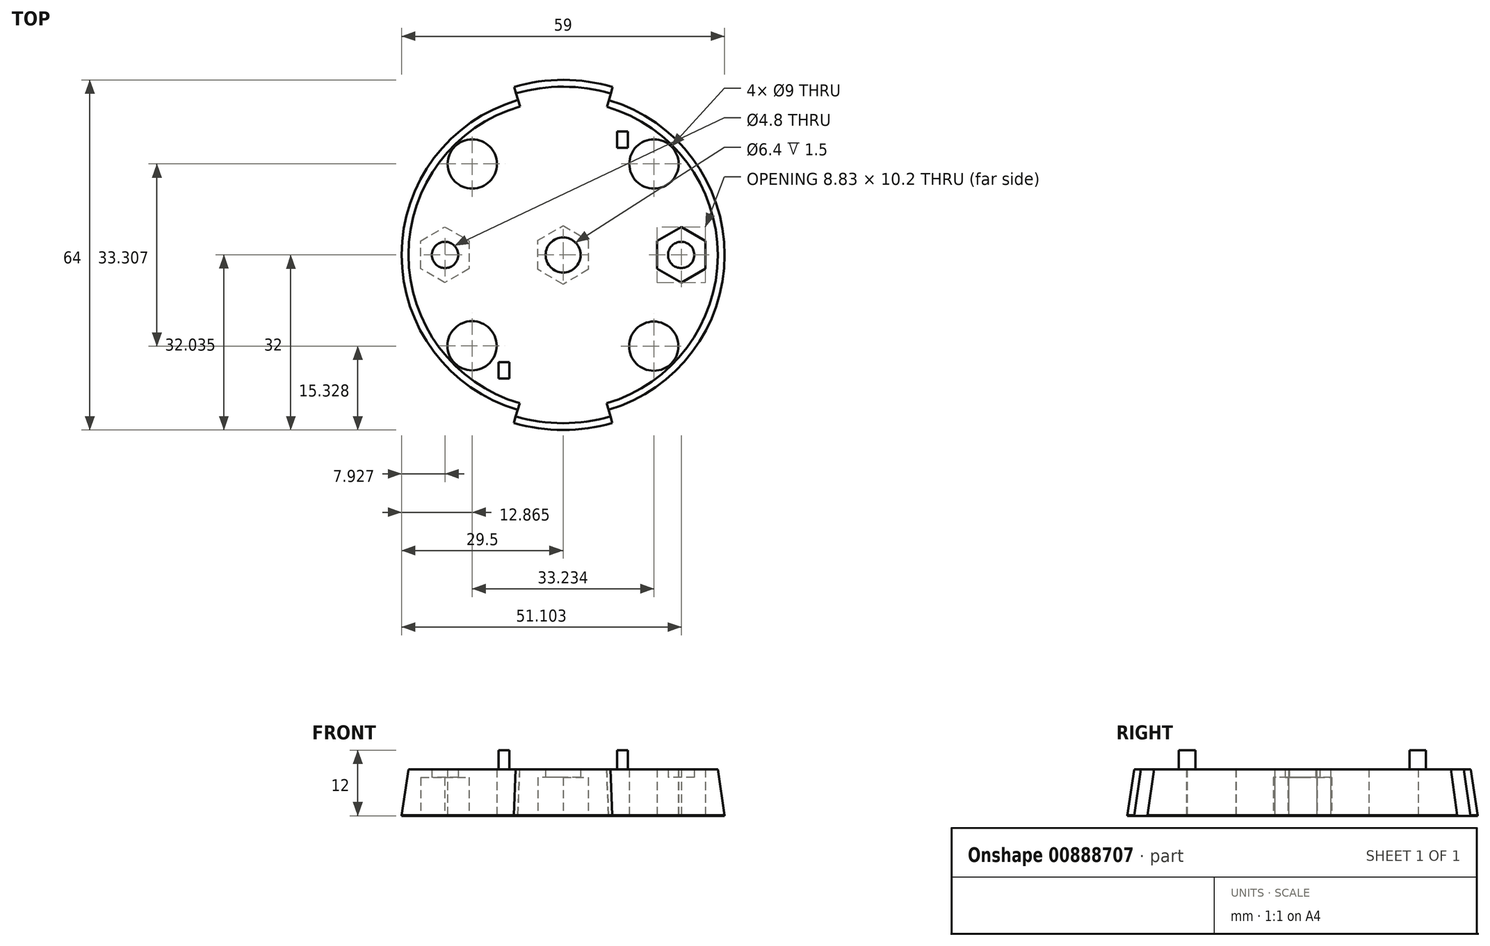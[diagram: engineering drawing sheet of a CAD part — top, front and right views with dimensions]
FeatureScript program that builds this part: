
annotation { "Feature Type Name" : "Feature", "Feature Type Description" : "" }
export const myFeature = defineFeature(function(context is Context, id is Id, definition is map)
    precondition{}
    {
        {
            var Q0;
            Q0=qCreatedBy(makeId("Top.planeOp"),FACE);
            var sketch = newSketch(context, id + "F0", { "sketchPlane" : qUnion([Q0])});
            skCircle(sketch, "E0", {"center": v(0, 0) * mm, "radius": 32 * mm});
            skCircle(sketch, "E1.cCircle", {"center": v(0, 0) * mm, "radius": 4.62 * mm, "construction": true});
            skLineSegment(sketch, "E1.0", {"start": v(4.62, 2.67) * mm, "end": v(4.62, -2.67) * mm});
            skLineSegment(sketch, "E1.1", {"start": v(4.62, -2.67) * mm, "end": v(0, -5.34) * mm});
            skLineSegment(sketch, "E1.2", {"start": v(0, -5.34) * mm, "end": v(-4.63, -2.67) * mm});
            skLineSegment(sketch, "E1.3", {"start": v(-4.62, -2.67) * mm, "end": v(-4.62, 2.67) * mm});
            skLineSegment(sketch, "E1.4", {"start": v(-4.63, 2.67) * mm, "end": v(0, 5.34) * mm});
            skLineSegment(sketch, "E1.5", {"start": v(0, 5.34) * mm, "end": v(4.62, 2.67) * mm});
            skPoint(sketch, "E1.0.midPoint", {"position": v(4.62, 0) * mm});
            skCircle(sketch, "E2", {"center": v(0, 0) * mm, "radius": 3.2 * mm});
            skCircle(sketch, "E3", {"center": v(0, 0) * mm, "radius": 29.5 * mm});
            skCircle(sketch, "E4", {"center": v(-29.5, 0) * mm, "radius": 4.3 * mm, "construction": true});
            skLineSegment(sketch, "E5", {"start": v(0, 5.34) * mm, "end": v(0, -5.34) * mm, "construction": true});
            skLineSegment(sketch, "E6", {"start": v(0, 0) * mm, "end": v(-35.07, 35.15) * mm, "construction": true});
            skLineSegment(sketch, "E7", {"start": v(0, 0) * mm, "end": v(-62.76, 0.07) * mm, "construction": true});
            skLineSegment(sketch, "E8", {"start": v(0, -32) * mm, "end": v(0, -45.25) * mm, "construction": true});
            skLineSegment(sketch, "E9", {"start": v(0, -45.25) * mm, "end": v(-9, -45.25) * mm, "construction": true});
            skLineSegment(sketch, "E10", {"start": v(-9, -45.25) * mm, "end": v(-9, -28.1) * mm, "construction": true});
            skCircle(sketch, "E11", {"center": v(-29.5, 0) * mm, "radius": 4 * mm, "construction": true});
            skCircle(sketch, "E12", {"center": v(-20.84, 20.88) * mm, "radius": 2.5 * mm, "construction": true});
            skLineSegment(sketch, "E13", {"start": v(-19.07, 19.11) * mm, "end": v(-16.6, 16.64) * mm, "construction": true});
            skCircle(sketch, "E14.MirrorC", {"center": v(16.6, 16.64) * mm, "radius": 4.5 * mm});
            skCircle(sketch, "E15.MirrorC", {"center": v(16.56, -16.67) * mm, "radius": 4.5 * mm});
            skLineSegment(sketch, "E16", {"start": v(-9, -30.7) * mm, "end": v(0, 0) * mm, "construction": true});
            skLineSegment(sketch, "E17", {"start": v(-9, -30.7) * mm, "end": v(-8.3, -28.3) * mm});
            skLineSegment(sketch, "E18.MirrorCS", {"start": v(9, -30.7) * mm, "end": v(8.3, -28.3) * mm});
            skLineSegment(sketch, "E19.MirrorCS", {"start": v(9.07, 30.69) * mm, "end": v(8.36, 28.3) * mm});
            skLineSegment(sketch, "E20.MirrorCS", {"start": v(-8.93, 30.73) * mm, "end": v(-8.23, 28.33) * mm});
            skLineSegment(sketch, "E21", {"start": v(-21.6, 0.03) * mm, "end": v(-21.57, -10.48) * mm, "construction": true});
            skCircle(sketch, "E22", {"center": v(-16.6, 16.64) * mm, "radius": 4.5 * mm});
            skCircle(sketch, "E23.MirrorC", {"center": v(-16.64, -16.6) * mm, "radius": 4.5 * mm});
            skPoint(sketch, "E24.0.midPoint", {"position": v(-17.25, -2.43) * mm});
            skCircle(sketch, "E25.cCircle", {"center": v(-21.6, 0.03) * mm, "radius": 5.1 * mm, "construction": true});
            skLineSegment(sketch, "E25.0", {"start": v(-21.6, 5.13) * mm, "end": v(-17.19, 2.58) * mm});
            skLineSegment(sketch, "E25.1", {"start": v(-17.19, 2.58) * mm, "end": v(-17.19, -2.52) * mm});
            skLineSegment(sketch, "E25.2", {"start": v(-17.19, -2.52) * mm, "end": v(-21.6, -5.07) * mm});
            skLineSegment(sketch, "E25.3", {"start": v(-21.6, -5.07) * mm, "end": v(-26.02, -2.52) * mm});
            skLineSegment(sketch, "E25.4", {"start": v(-26.02, -2.52) * mm, "end": v(-26.02, 2.58) * mm});
            skLineSegment(sketch, "E25.5", {"start": v(-26.02, 2.58) * mm, "end": v(-21.6, 5.13) * mm});
            skLineSegment(sketch, "E26.MirrorCS", {"start": v(26.02, 2.58) * mm, "end": v(21.6, 5.13) * mm});
            skLineSegment(sketch, "E27.MirrorCS", {"start": v(21.6, 5.13) * mm, "end": v(17.19, 2.58) * mm});
            skLineSegment(sketch, "E28.MirrorCS", {"start": v(17.19, -2.52) * mm, "end": v(21.6, -5.07) * mm});
            skLineSegment(sketch, "E29.MirrorCS", {"start": v(17.19, 2.58) * mm, "end": v(17.19, -2.52) * mm});
            skLineSegment(sketch, "E30.MirrorCS", {"start": v(21.6, -5.07) * mm, "end": v(26.02, -2.52) * mm});
            skLineSegment(sketch, "E31.MirrorCS", {"start": v(26.02, -2.52) * mm, "end": v(26.02, 2.58) * mm});
            skSolve(sketch);
        }
        {
            var Q0;
            Q0=makeQuery(id+"F0.imprint","IMPRINT",FACE,{"disambiguationData":[TD([[makeQuery(id+"F0.imprint","IMPRINT",EDGE,{"derivedFrom":sQuery(id+"F0.wireOp",EDGE,"E1.0")}),1.0]])]});
            var Q1;
            {var subQ0=sQuery(id+"F0.wireOp",EDGE,"0532653d-6b39-4b15-b1f7-16973653ea9d0.MirrorCS");Q1=makeQuery(id+"F0.imprint","IMPRINT",FACE,{"disambiguationData":[TD([[makeQuery(id+"F0.imprint","IMPRINT",EDGE,{"derivedFrom":subQ0}),-1.0]])]});}
            var Q2;
            {var subQ0=sQuery(id+"F0.wireOp",EDGE,"nI7ypJ2F-p2nV-rztm-eMBW-cwVU348m9M7Z");Q2=makeQuery(id+"F0.imprint","IMPRINT",FACE,{"disambiguationData":[TD([[makeQuery(id+"F0.imprint","IMPRINT",EDGE,{"derivedFrom":subQ0}),1.0]])]});}
            var Q3;
            {var subQ0=sQuery(id+"F0.wireOp",EDGE,"E19.MirrorCS");Q3=makeQuery(id+"F0.imprint","IMPRINT",FACE,{"disambiguationData":[TD([[makeQuery(id+"F0.imprint","IMPRINT",EDGE,{"derivedFrom":subQ0}),-1.0]])]});}
            var Q4;
            {var subQ0=sQuery(id+"F0.wireOp",EDGE,"E17");Q4=makeQuery(id+"F0.imprint","IMPRINT",FACE,{"disambiguationData":[TD([[makeQuery(id+"F0.imprint","IMPRINT",EDGE,{"derivedFrom":subQ0}),-1.0]])]});}
            extrude(context, id + "F1", {"entities" : qUnion([Q0, Q1, Q2, Q3, Q4]), "depth" : 4 * mm, "offsetDistance" : 25 * mm});
        }
        {
            var Q0;
            Q0=makeQuery(id+"F1.opExtrude","CAP_FACE",FACE,{"disambiguationData":[OSD([sQuery(id+"F0.wireOp",EDGE,"E0"),sQuery(id+"F0.wireOp",EDGE,"E1.0"),sQuery(id+"F0.wireOp",EDGE,"E1.1"),sQuery(id+"F0.wireOp",EDGE,"E1.2"),sQuery(id+"F0.wireOp",EDGE,"E1.3"),sQuery(id+"F0.wireOp",EDGE,"E1.4"),sQuery(id+"F0.wireOp",EDGE,"E1.5"),sQuery(id+"F0.wireOp",EDGE,"E3"),sQuery(id+"F0.wireOp",EDGE,"c5f974a7-216e-424f-9550-b7bfad47bf20.0"),sQuery(id+"F0.wireOp",EDGE,"c5f974a7-216e-424f-9550-b7bfad47bf20.1"),sQuery(id+"F0.wireOp",EDGE,"c5f974a7-216e-424f-9550-b7bfad47bf20.2"),sQuery(id+"F0.wireOp",EDGE,"c5f974a7-216e-424f-9550-b7bfad47bf20.3"),sQuery(id+"F0.wireOp",EDGE,"c5f974a7-216e-424f-9550-b7bfad47bf20.4"),sQuery(id+"F0.wireOp",EDGE,"c5f974a7-216e-424f-9550-b7bfad47bf20.5"),sQuery(id+"F0.wireOp",EDGE,"nI7ypJ2F-p2nV-rztm-eMBW-cwVU348m9M7Z"),sQuery(id+"F0.wireOp",EDGE,"Z7XU2lvm-BlL3-PO4m-le69-E0NbLayMHUxe"),sQuery(id+"F0.wireOp",EDGE,"0532653d-6b39-4b15-b1f7-16973653ea9d0.MirrorCS"),sQuery(id+"F0.wireOp",EDGE,"d8052036-d010-4aef-a763-387b3686d8280.MirrorCS"),sQuery(id+"F0.wireOp",EDGE,"8ae0d3ce-86ad-4dfc-b9ce-d51649e9d0df0.MirrorCS"),sQuery(id+"F0.wireOp",EDGE,"461546e5-d8ef-42f4-ba26-d96cefa50c180.MirrorCS"),sQuery(id+"F0.wireOp",EDGE,"039d2f36-9cdf-4b2a-a9c5-0ec75abb23c90.MirrorCS"),sQuery(id+"F0.wireOp",EDGE,"8f7f1927-4131-468a-8d37-5ebb414fe5330.MirrorCS"),sQuery(id+"F0.wireOp",EDGE,"819d87e7-4fc0-4cc7-8b2e-3353cf5893e90.MirrorCS"),sQuery(id+"F0.wireOp",EDGE,"afff235e-c4fe-4a88-b5ed-a0414b9d12000.MirrorCS"),sQuery(id+"F0.wireOp",EDGE,"5HerYpeO-Iayk-iDGq-pvE3-skKb7w50cPca"),sQuery(id+"F0.wireOp",EDGE,"E14.MirrorC"),sQuery(id+"F0.wireOp",EDGE,"dda9c2b3-7f4d-4ca0-a861-7ab3f66567b30.MirrorC"),sQuery(id+"F0.wireOp",EDGE,"E15.MirrorC")])],"isStart":false});
            var sketch = newSketch(context, id + "F2", { "sketchPlane" : qUnion([Q0])});
            skLineSegment(sketch, "E32", {"start": v(0, 0) * mm, "end": v(0, 7.5) * mm, "construction": true});
            skSolve(sketch);
        }
        {
            var Q0;
            Q0=makeQuery(id+"F2.imprint","IMPRINT",FACE,{"disambiguationData":[TD([[makeQuery(id+"F2.imprint","IMPRINT",EDGE,{"derivedFrom":makeQuery(id+"F1.opExtrude","CAP_EDGE",EDGE,{"disambiguationData":[OSD([sQuery(id+"F0.wireOp",EDGE,"E1.0")])],"isStart":false})}),1.0]])]});
            var Q1;
            Q1=makeQuery(id+"F2.imprint","IMPRINT",FACE,{"disambiguationData":[TD([[makeQuery(id+"F2.imprint","IMPRINT",EDGE,{"derivedFrom":sQuery(id+"F2.wireOp",EDGE,"Fbujtv53-bloy-TrV9-Xnpe-BXHdm6c1psMM")}),-1.0]])]});
            extrude(context, id + "F3", {"entities" : qUnion([Q0, Q1]), "operationType" : NewBodyOperationType.ADD, "depth" : 3 * mm, "offsetDistance" : 25 * mm});
        }
        {
            var Q0;
            Q0=makeQuery(id+"F3.opExtrude","CAP_FACE",FACE,{"disambiguationData":[OSD([sQuery(id+"F0.wireOp",EDGE,"E0"),sQuery(id+"F0.wireOp",EDGE,"E1.0"),sQuery(id+"F0.wireOp",EDGE,"E1.1"),sQuery(id+"F0.wireOp",EDGE,"E1.2"),sQuery(id+"F0.wireOp",EDGE,"E1.3"),sQuery(id+"F0.wireOp",EDGE,"E1.4"),sQuery(id+"F0.wireOp",EDGE,"E1.5"),sQuery(id+"F0.wireOp",EDGE,"E3"),sQuery(id+"F0.wireOp",EDGE,"nI7ypJ2F-p2nV-rztm-eMBW-cwVU348m9M7Z"),sQuery(id+"F0.wireOp",EDGE,"Z7XU2lvm-BlL3-PO4m-le69-E0NbLayMHUxe"),sQuery(id+"F0.wireOp",EDGE,"0532653d-6b39-4b15-b1f7-16973653ea9d0.MirrorCS"),sQuery(id+"F0.wireOp",EDGE,"d8052036-d010-4aef-a763-387b3686d8280.MirrorCS"),sQuery(id+"F0.wireOp",EDGE,"5HerYpeO-Iayk-iDGq-pvE3-skKb7w50cPca"),sQuery(id+"F0.wireOp",EDGE,"E14.MirrorC"),sQuery(id+"F0.wireOp",EDGE,"dda9c2b3-7f4d-4ca0-a861-7ab3f66567b30.MirrorC"),sQuery(id+"F0.wireOp",EDGE,"E15.MirrorC"),sQuery(id+"F2.wireOp",EDGE,"Fbujtv53-bloy-TrV9-Xnpe-BXHdm6c1psMM"),sQuery(id+"F2.wireOp",EDGE,"1dfd9ed7-96bc-4922-abb2-6f56f110bf680.MirrorC")])],"isStart":false});
            var sketch = newSketch(context, id + "F4", { "sketchPlane" : qUnion([Q0])});
            skCircle(sketch, "E33", {"center": v(0, 0) * mm, "radius": 3.2 * mm});
            skCircle(sketch, "E34", {"center": v(-21.57, 0) * mm, "radius": 2.4 * mm});
            skCircle(sketch, "E35.MirrorC", {"center": v(21.57, 0) * mm, "radius": 2.4 * mm});
            skSolve(sketch);
        }
        {
            var Q0;
            Q0=makeQuery(id+"F4.imprint","IMPRINT",FACE,{"disambiguationData":[TD([[makeQuery(id+"F4.imprint","IMPRINT",EDGE,{"derivedFrom":makeQuery(id+"F3.opExtrude","CAP_EDGE",EDGE,{"disambiguationData":[OSD([sQuery(id+"F0.wireOp",EDGE,"E1.0")])],"isStart":false})}),1.0]])]});
            var Q1;
            Q1=makeQuery(id+"F4.imprint","IMPRINT",FACE,{"disambiguationData":[TD([[makeQuery(id+"F4.imprint","IMPRINT",EDGE,{"derivedFrom":sQuery(id+"F4.wireOp",EDGE,"E33")}),-1.0]])]});
            var Q2;
            Q2=makeQuery(id+"F4.imprint","IMPRINT",FACE,{"disambiguationData":[TD([[makeQuery(id+"F4.imprint","IMPRINT",EDGE,{"derivedFrom":sQuery(id+"F4.wireOp",EDGE,"E34")}),-1.0]])]});
            var Q3;
            Q3=makeQuery(id+"F4.imprint","IMPRINT",FACE,{"disambiguationData":[TD([[makeQuery(id+"F4.imprint","IMPRINT",EDGE,{"derivedFrom":sQuery(id+"F4.wireOp",EDGE,"E35.MirrorC")}),1.0]])]});
            extrude(context, id + "F5", {"entities" : qUnion([Q0, Q1, Q2, Q3]), "operationType" : NewBodyOperationType.ADD, "depth" : 1.5 * mm, "offsetDistance" : 25 * mm});
        }
        {
            var Q0;
            Q0=makeQuery(id+"F5.opExtrude","CAP_FACE",FACE,{"disambiguationData":[OSD([sQuery(id+"F0.wireOp",EDGE,"E0"),sQuery(id+"F0.wireOp",EDGE,"E3"),sQuery(id+"F0.wireOp",EDGE,"nI7ypJ2F-p2nV-rztm-eMBW-cwVU348m9M7Z"),sQuery(id+"F0.wireOp",EDGE,"Z7XU2lvm-BlL3-PO4m-le69-E0NbLayMHUxe"),sQuery(id+"F0.wireOp",EDGE,"0532653d-6b39-4b15-b1f7-16973653ea9d0.MirrorCS"),sQuery(id+"F0.wireOp",EDGE,"d8052036-d010-4aef-a763-387b3686d8280.MirrorCS"),sQuery(id+"F0.wireOp",EDGE,"5HerYpeO-Iayk-iDGq-pvE3-skKb7w50cPca"),sQuery(id+"F0.wireOp",EDGE,"E14.MirrorC"),sQuery(id+"F0.wireOp",EDGE,"dda9c2b3-7f4d-4ca0-a861-7ab3f66567b30.MirrorC"),sQuery(id+"F0.wireOp",EDGE,"E15.MirrorC"),sQuery(id+"F2.wireOp",EDGE,"Fbujtv53-bloy-TrV9-Xnpe-BXHdm6c1psMM"),sQuery(id+"F2.wireOp",EDGE,"1dfd9ed7-96bc-4922-abb2-6f56f110bf680.MirrorC"),sQuery(id+"F4.wireOp",EDGE,"E33")])],"isStart":false});
            var sketch = newSketch(context, id + "F6", { "sketchPlane" : qUnion([Q0])});
            skLineSegment(sketch, "E36.bottom", {"start": v(-7.77, -24.26) * mm, "end": v(-10.91, -23.26) * mm, "construction": true});
            skLineSegment(sketch, "E36.top", {"start": v(-6.55, -20.45) * mm, "end": v(-9.7, -19.45) * mm, "construction": true});
            skLineSegment(sketch, "E36.right", {"start": v(-10.91, -23.26) * mm, "end": v(-9.7, -19.45) * mm, "construction": true});
            skLineSegment(sketch, "E37", {"start": v(0, 0) * mm, "end": v(12.53, -4.03) * mm, "construction": true});
            skLineSegment(sketch, "E38.trimOffspring", {"start": v(0.03, 0) * mm, "end": v(-10.38, -32.38) * mm});
            skLineSegment(sketch, "E39", {"start": v(-8.08, -25.24) * mm, "end": v(-4.2, -25.24) * mm, "construction": true});
            skCircle(sketch, "E40", {"center": v(-9, -28.07) * mm, "radius": 4 * mm, "construction": true});
            skLineSegment(sketch, "E41", {"start": v(-6.55, -20.45) * mm, "end": v(-7.77, -24.26) * mm, "construction": true});
            skCircle(sketch, "E42", {"center": v(0.03, 0) * mm, "radius": 10 * mm, "construction": true});
            skLineSegment(sketch, "E43", {"start": v(-9, -28.07) * mm, "end": v(-9.98, 0) * mm, "construction": true});
            skLineSegment(sketch, "E44.bottom", {"start": v(-9.79, -19.58) * mm, "end": v(-11.79, -19.58) * mm});
            skLineSegment(sketch, "E44.top", {"start": v(-9.79, -22.58) * mm, "end": v(-11.79, -22.58) * mm});
            skLineSegment(sketch, "E44.right", {"start": v(-11.79, -19.58) * mm, "end": v(-11.79, -22.58) * mm});
            skLineSegment(sketch, "E45", {"start": v(-9.79, -19.58) * mm, "end": v(-9.79, -22.58) * mm});
            skLineSegment(sketch, "E46.MirrorCS", {"start": v(-3.4, -21.63) * mm, "end": v(-1.77, -22.8) * mm});
            skLineSegment(sketch, "E47.MirrorCS", {"start": v(-1.77, -22.8) * mm, "end": v(-3.52, -25.24) * mm});
            skLineSegment(sketch, "E48.MirrorCS", {"start": v(-5.14, -24.07) * mm, "end": v(-3.52, -25.24) * mm});
            skLineSegment(sketch, "E49.MirrorCS", {"start": v(-3.4, -21.63) * mm, "end": v(-5.14, -24.07) * mm});
            skLineSegment(sketch, "E50.MirrorCS", {"start": v(9.85, 19.56) * mm, "end": v(11.85, 19.56) * mm});
            skLineSegment(sketch, "E51.MirrorCS", {"start": v(9.85, 19.56) * mm, "end": v(9.85, 22.56) * mm});
            skLineSegment(sketch, "E52.MirrorCS", {"start": v(11.85, 19.56) * mm, "end": v(11.85, 22.56) * mm});
            skLineSegment(sketch, "E53", {"start": v(9.85, 22.56) * mm, "end": v(11.85, 22.56) * mm});
            skSolve(sketch);
        }
        {
            var Q0;
            Q0=makeQuery(id+"F6.imprint","IMPRINT",FACE,{"disambiguationData":[TD([[makeQuery(id+"F6.imprint","IMPRINT",EDGE,{"derivedFrom":sQuery(id+"F6.wireOp",EDGE,"E44.bottom")}),1.0]])]});
            var Q1;
            Q1=makeQuery(id+"F6.imprint","IMPRINT",FACE,{"disambiguationData":[TD([[makeQuery(id+"F6.imprint","IMPRINT",EDGE,{"derivedFrom":sQuery(id+"F6.wireOp",EDGE,"E50.MirrorCS")}),1.0]])]});
            extrude(context, id + "F7", {"entities" : qUnion([Q0, Q1]), "operationType" : NewBodyOperationType.ADD, "depth" : 3.5 * mm, "offsetDistance" : 25 * mm});
        }
        {
            var Q0;
            {var subQ0=sQuery(id+"F0.wireOp",EDGE,"E3");Q0=makeQuery(id+"F5.opExtrude","CAP_EDGE",EDGE,{"disambiguationData":[OSD([subQ0]),TDD([makeQuery(id+"F4.imprint","IMPRINT",EDGE,{"derivedFrom":makeQuery(id+"F3.opExtrude","CAP_EDGE",EDGE,{"disambiguationData":[OSD([subQ0]),TDD([makeQuery(id+"F2.imprint","IMPRINT",EDGE,{"derivedFrom":makeQuery(id+"F1.opExtrude","CAP_EDGE",EDGE,{"disambiguationData":[OSD([subQ0]),TDD([makeQuery(id+"F0.imprint","IMPRINT",EDGE,{"disambiguationData":[TD([[makeQuery(id+"F0.imprint","INTERSECT",VERTEX,{"derivedFrom":[subQ0,sQuery(id+"F0.wireOp",EDGE,"Z7XU2lvm-BlL3-PO4m-le69-E0NbLayMHUxe")]}),-1.0]])],"derivedFrom":subQ0})])],"isStart":false})})])],"isStart":false})})])],"isStart":false});}
            var Q1;
            {var subQ0=sQuery(id+"F0.wireOp",EDGE,"E3");Q1=makeQuery(id+"F5.opExtrude","CAP_EDGE",EDGE,{"disambiguationData":[OSD([subQ0]),TDD([makeQuery(id+"F4.imprint","IMPRINT",EDGE,{"derivedFrom":makeQuery(id+"F3.opExtrude","CAP_EDGE",EDGE,{"disambiguationData":[OSD([subQ0]),TDD([makeQuery(id+"F2.imprint","IMPRINT",EDGE,{"derivedFrom":makeQuery(id+"F1.opExtrude","CAP_EDGE",EDGE,{"disambiguationData":[OSD([subQ0]),TDD([makeQuery(id+"F0.imprint","IMPRINT",EDGE,{"disambiguationData":[TD([[makeQuery(id+"F0.imprint","INTERSECT",VERTEX,{"derivedFrom":[subQ0,sQuery(id+"F0.wireOp",EDGE,"nI7ypJ2F-p2nV-rztm-eMBW-cwVU348m9M7Z")]}),1.0]])],"derivedFrom":subQ0})])],"isStart":false})})])],"isStart":false})})])],"isStart":false});}
            var Q2;
            {var subQ0=sQuery(id+"F0.wireOp",EDGE,"E0");Q2=makeQuery(id+"F5.opExtrude","CAP_EDGE",EDGE,{"disambiguationData":[OSD([subQ0]),TDD([makeQuery(id+"F4.imprint","IMPRINT",EDGE,{"derivedFrom":makeQuery(id+"F3.opExtrude","CAP_EDGE",EDGE,{"disambiguationData":[OSD([subQ0]),TDD([makeQuery(id+"F2.imprint","IMPRINT",EDGE,{"derivedFrom":makeQuery(id+"F1.opExtrude","CAP_EDGE",EDGE,{"disambiguationData":[OSD([subQ0]),TDD([makeQuery(id+"F0.imprint","IMPRINT",EDGE,{"disambiguationData":[TD([[makeQuery(id+"F0.imprint","INTERSECT",VERTEX,{"derivedFrom":[subQ0,sQuery(id+"F0.wireOp",EDGE,"nI7ypJ2F-p2nV-rztm-eMBW-cwVU348m9M7Z")]}),-1.0]])],"derivedFrom":subQ0})])],"isStart":false})})])],"isStart":false})})])],"isStart":false});}
            var Q3;
            {var subQ0=sQuery(id+"F0.wireOp",EDGE,"E0");Q3=makeQuery(id+"F5.opExtrude","CAP_EDGE",EDGE,{"disambiguationData":[OSD([subQ0]),TDD([makeQuery(id+"F4.imprint","IMPRINT",EDGE,{"derivedFrom":makeQuery(id+"F3.opExtrude","CAP_EDGE",EDGE,{"disambiguationData":[OSD([subQ0]),TDD([makeQuery(id+"F2.imprint","IMPRINT",EDGE,{"derivedFrom":makeQuery(id+"F1.opExtrude","CAP_EDGE",EDGE,{"disambiguationData":[OSD([subQ0]),TDD([makeQuery(id+"F0.imprint","IMPRINT",EDGE,{"disambiguationData":[TD([[makeQuery(id+"F0.imprint","INTERSECT",VERTEX,{"derivedFrom":[subQ0,sQuery(id+"F0.wireOp",EDGE,"0532653d-6b39-4b15-b1f7-16973653ea9d0.MirrorCS")]}),1.0]])],"derivedFrom":subQ0})])],"isStart":false})})])],"isStart":false})})])],"isStart":false});}
            chamfer(context, id + "F8", {"entities" : qUnion([Q0, Q1, Q2, Q3]), "chamferType" : ChamferType.TWO_OFFSETS, "width1" : 1.25 * mm, "oppositeDirection" : false, "width2" : 8.4 * mm, "tangentPropagation" : true});
        }
    });
